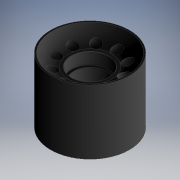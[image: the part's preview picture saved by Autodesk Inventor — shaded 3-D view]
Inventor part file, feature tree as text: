
AUTODESK INVENTOR PART (.ipt)
format: ipt  version: 2019.4 (Build 234330000, 330)  size: 347,648 bytes
history: native  units: mm
features: sketch x5, extrude x4, mirror x2, fillet x2, revolve x1, pattern_circular x1, plane x1
ambient origin geometry x8: Origin, YZ Plane, XZ Plane, XY Plane, X Axis, Y Axis, Z Axis, Center Point
bodies: Solid1 (feature_tree)
feature tree (16):
  extrude  "Extrusion1"  Depth=19.0mm
  extrude  "Extrusion2"  Depth=31.7mm
  revolve  "Revolution1"  [1 undecoded]
  mirror  "Mirror2"
  fillet  "Fillet1"  Radius=100.0mm
  extrude  "Extrusion4"  Depth=30.0mm
  pattern_circular  "Circular Pattern1"  [2 undecoded]
  plane  "Work Plane1"
  extrude  "Extrusion5"  Depth=0.2mm
  mirror  "Mirror3"
  fillet  "Fillet5"  Radius=12.0mm
  sketch  "Sketch1"  dims[d0=38.0mm d1=0.0mm d2=19.0mm]
  sketch  "Sketch2"  dims[d3=56.0mm d4=0.0mm d8=31.7mm]
  sketch  "Sketch4"  dims[d9=5.8mm d10=60.75mm d11=0.0mm d12=100.0mm d13=360.0deg]
  sketch  "Sketch5"  dims[d15=46.6mm d18=30.0mm]
  sketch  "Sketch7"  dims[d19=90.0deg d20=10.0mm d31=44.8mm d32=12.0mm d33=5.0mm d34=22.0mm d35=20.0mm d36=0.0mm d37=0.2mm]
note: 3 required parameter values undecoded (feature->parameter linkage not recoverable at this tier; creation-order binding heuristic only, values carry confidence <= 0.55)